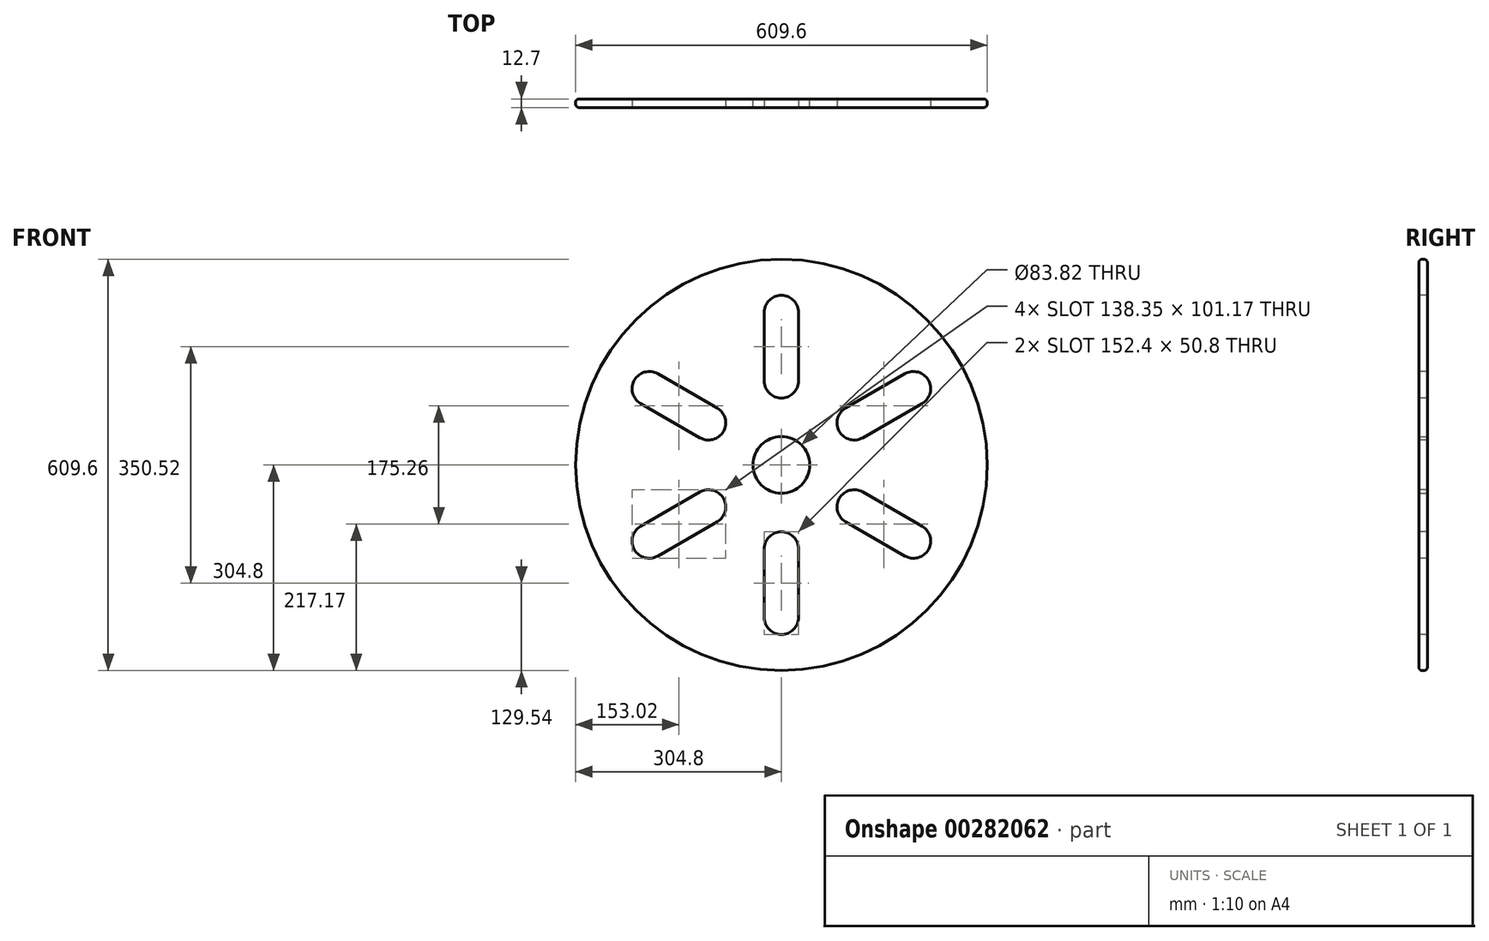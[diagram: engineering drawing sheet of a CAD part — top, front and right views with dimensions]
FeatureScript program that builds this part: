
annotation { "Feature Type Name" : "Feature", "Feature Type Description" : "" }
export const myFeature = defineFeature(function(context is Context, id is Id, definition is map)
    precondition{}
    {
        {
            var Q0;
            Q0=qCreatedBy(makeId("Front.planeOp"),FACE);
            var sketch = newSketch(context, id + "F0", { "sketchPlane" : qUnion([Q0])});
            skCircle(sketch, "E0", {"center": v(0, 0) * mm, "radius": 304.8 * mm});
            skCircle(sketch, "E1", {"center": v(0, 0) * mm, "radius": 41.91 * mm});
            skSolve(sketch);
        }
        {
            var Q0;
            Q0=makeQuery(id+"F0.imprint","IMPRINT",FACE,{"disambiguationData":[TD([[makeQuery(id+"F0.imprint","IMPRINT",EDGE,{"derivedFrom":sQuery(id+"F0.wireOp",EDGE,"E0")}),1.0]])]});
            extrude(context, id + "F1", {"entities" : qUnion([Q0]), "depth" : 12.7 * mm});
        }
        {
            var Q0;
            Q0=makeQuery(id+"F1.opExtrude","CAP_FACE",FACE,{"disambiguationData":[OSD([sQuery(id+"F0.wireOp",EDGE,"E0"),sQuery(id+"F0.wireOp",EDGE,"E1")])],"isStart":false});
            var sketch = newSketch(context, id + "F2", { "sketchPlane" : qUnion([Q0])});
            skLineSegment(sketch, "E2.left", {"start": v(-25.4, 124.46) * mm, "end": v(-25.4, 226.06) * mm});
            skLineSegment(sketch, "E2.right", {"start": v(25.4, 124.46) * mm, "end": v(25.4, 226.06) * mm});
            skPoint(sketch, "E2.middle", {"position": v(0, 175.26) * mm});
            skArc(sketch, "E3", {"start": v(25.4, 226.06) * mm, "mid": v(0, 251.46) * mm, "end": v(-25.4, 226.06) * mm});
            skArc(sketch, "E4", {"start": v(-25.4, 124.46) * mm, "mid": v(0, 99.06) * mm, "end": v(25.4, 124.46) * mm});
            skArc(sketch, "E5.1.0", {"start": v(-120.49, 40.23) * mm, "mid": v(-85.79, 49.53) * mm, "end": v(-95.09, 84.23) * mm});
            skLineSegment(sketch, "E5.1.1", {"start": v(-95.09, 84.23) * mm, "end": v(-183.07, 135.03) * mm});
            skLineSegment(sketch, "E5.1.2", {"start": v(-120.49, 40.23) * mm, "end": v(-208.47, 91.03) * mm});
            skArc(sketch, "E5.1.3", {"start": v(-183.07, 135.03) * mm, "mid": v(-217.77, 125.73) * mm, "end": v(-208.47, 91.03) * mm});
            skArc(sketch, "E5.2.0", {"start": v(-95.09, -84.23) * mm, "mid": v(-85.79, -49.53) * mm, "end": v(-120.49, -40.23) * mm});
            skLineSegment(sketch, "E5.2.1", {"start": v(-120.49, -40.23) * mm, "end": v(-208.47, -91.03) * mm});
            skLineSegment(sketch, "E5.2.2", {"start": v(-95.09, -84.23) * mm, "end": v(-183.07, -135.03) * mm});
            skArc(sketch, "E5.2.3", {"start": v(-208.47, -91.03) * mm, "mid": v(-217.77, -125.73) * mm, "end": v(-183.07, -135.03) * mm});
            skPoint(sketch, "E5.center", {"position": v(0, 0) * mm});
            skLineSegment(sketch, "E6", {"start": v(0, 304.8) * mm, "end": v(0, -304.8) * mm, "construction": true});
            skArc(sketch, "E7.2.3.0", {"start": v(25.4, -124.46) * mm, "mid": v(0, -99.06) * mm, "end": v(-25.4, -124.46) * mm});
            skLineSegment(sketch, "E7.4.3.0", {"start": v(-25.4, -124.46) * mm, "end": v(-25.4, -226.06) * mm});
            skLineSegment(sketch, "E7.7.3.0", {"start": v(25.4, -124.46) * mm, "end": v(25.4, -226.06) * mm});
            skArc(sketch, "E7.10.3.0", {"start": v(-25.4, -226.06) * mm, "mid": v(0, -251.46) * mm, "end": v(25.4, -226.06) * mm});
            skArc(sketch, "E8.2.4.0", {"start": v(120.49, -40.23) * mm, "mid": v(85.79, -49.53) * mm, "end": v(95.09, -84.23) * mm});
            skLineSegment(sketch, "E8.4.4.0", {"start": v(95.09, -84.23) * mm, "end": v(183.07, -135.03) * mm});
            skLineSegment(sketch, "E8.7.4.0", {"start": v(120.49, -40.23) * mm, "end": v(208.47, -91.03) * mm});
            skArc(sketch, "E8.10.4.0", {"start": v(183.07, -135.03) * mm, "mid": v(217.77, -125.73) * mm, "end": v(208.47, -91.03) * mm});
            skArc(sketch, "E9.2.5.0", {"start": v(95.09, 84.23) * mm, "mid": v(85.79, 49.53) * mm, "end": v(120.49, 40.23) * mm});
            skLineSegment(sketch, "E9.4.5.0", {"start": v(120.49, 40.23) * mm, "end": v(208.47, 91.03) * mm});
            skLineSegment(sketch, "E9.7.5.0", {"start": v(95.09, 84.23) * mm, "end": v(183.07, 135.03) * mm});
            skArc(sketch, "E9.10.5.0", {"start": v(208.47, 91.03) * mm, "mid": v(217.77, 125.73) * mm, "end": v(183.07, 135.03) * mm});
            skSolve(sketch);
        }
        {
            var Q0;
            Q0=makeQuery(id+"F2.imprint","IMPRINT",FACE,{"disambiguationData":[TD([[makeQuery(id+"F2.imprint","IMPRINT",EDGE,{"derivedFrom":sQuery(id+"F2.wireOp",EDGE,"E2.left")}),-1.0]])]});
            var Q1;
            Q1=makeQuery(id+"F2.imprint","IMPRINT",FACE,{"disambiguationData":[TD([[makeQuery(id+"F2.imprint","IMPRINT",EDGE,{"derivedFrom":sQuery(id+"F2.wireOp",EDGE,"E5.5.0")}),1.0]])]});
            var Q2;
            Q2=makeQuery(id+"F2.imprint","IMPRINT",FACE,{"disambiguationData":[TD([[makeQuery(id+"F2.imprint","IMPRINT",EDGE,{"derivedFrom":sQuery(id+"F2.wireOp",EDGE,"E5.4.0")}),1.0]])]});
            var Q3;
            Q3=makeQuery(id+"F2.imprint","IMPRINT",FACE,{"disambiguationData":[TD([[makeQuery(id+"F2.imprint","IMPRINT",EDGE,{"derivedFrom":sQuery(id+"F2.wireOp",EDGE,"E5.3.0")}),1.0]])]});
            var Q4;
            Q4=makeQuery(id+"F2.imprint","IMPRINT",FACE,{"disambiguationData":[TD([[makeQuery(id+"F2.imprint","IMPRINT",EDGE,{"derivedFrom":sQuery(id+"F2.wireOp",EDGE,"E5.2.0")}),1.0]])]});
            var Q5;
            Q5=makeQuery(id+"F2.imprint","IMPRINT",FACE,{"disambiguationData":[TD([[makeQuery(id+"F2.imprint","IMPRINT",EDGE,{"derivedFrom":sQuery(id+"F2.wireOp",EDGE,"E5.1.0")}),1.0]])]});
            var Q6;
            Q6=makeQuery(id+"F2.imprint","IMPRINT",FACE,{"disambiguationData":[TD([[makeQuery(id+"F2.imprint","IMPRINT",EDGE,{"derivedFrom":sQuery(id+"F2.wireOp",EDGE,"E9.2.5.0")}),1.0]])]});
            var Q7;
            Q7=makeQuery(id+"F2.imprint","IMPRINT",FACE,{"disambiguationData":[TD([[makeQuery(id+"F2.imprint","IMPRINT",EDGE,{"derivedFrom":sQuery(id+"F2.wireOp",EDGE,"E8.2.4.0")}),1.0]])]});
            var Q8;
            Q8=makeQuery(id+"F2.imprint","IMPRINT",FACE,{"disambiguationData":[TD([[makeQuery(id+"F2.imprint","IMPRINT",EDGE,{"derivedFrom":sQuery(id+"F2.wireOp",EDGE,"E7.2.3.0")}),1.0]])]});
            extrude(context, id + "F3", {"entities" : qUnion([Q0, Q1, Q2, Q3, Q4, Q5, Q6, Q7, Q8]), "operationType" : NewBodyOperationType.REMOVE, "endBound" : BoundingType.THROUGH_ALL, "oppositeDirection" : true, "offsetDistance" : 25.4 * mm, "depth" : 25.4 * mm});
        }
        {
            var Q0;
            Q0=makeQuery(id+"F1.opExtrude","CAP_EDGE",EDGE,{"disambiguationData":[OSD([sQuery(id+"F0.wireOp",EDGE,"E0")])],"isStart":true});
            var Q1;
            Q1=makeQuery(id+"F1.opExtrude","CAP_EDGE",EDGE,{"disambiguationData":[OSD([sQuery(id+"F0.wireOp",EDGE,"E0")])],"isStart":false});
            fillet(context, id + "F4", {"entities" : qUnion([Q0, Q1]), "radius" : 5.08 * mm, "tangentPropagation" : true, "allowEdgeOverflow" : false});
        }
    });
